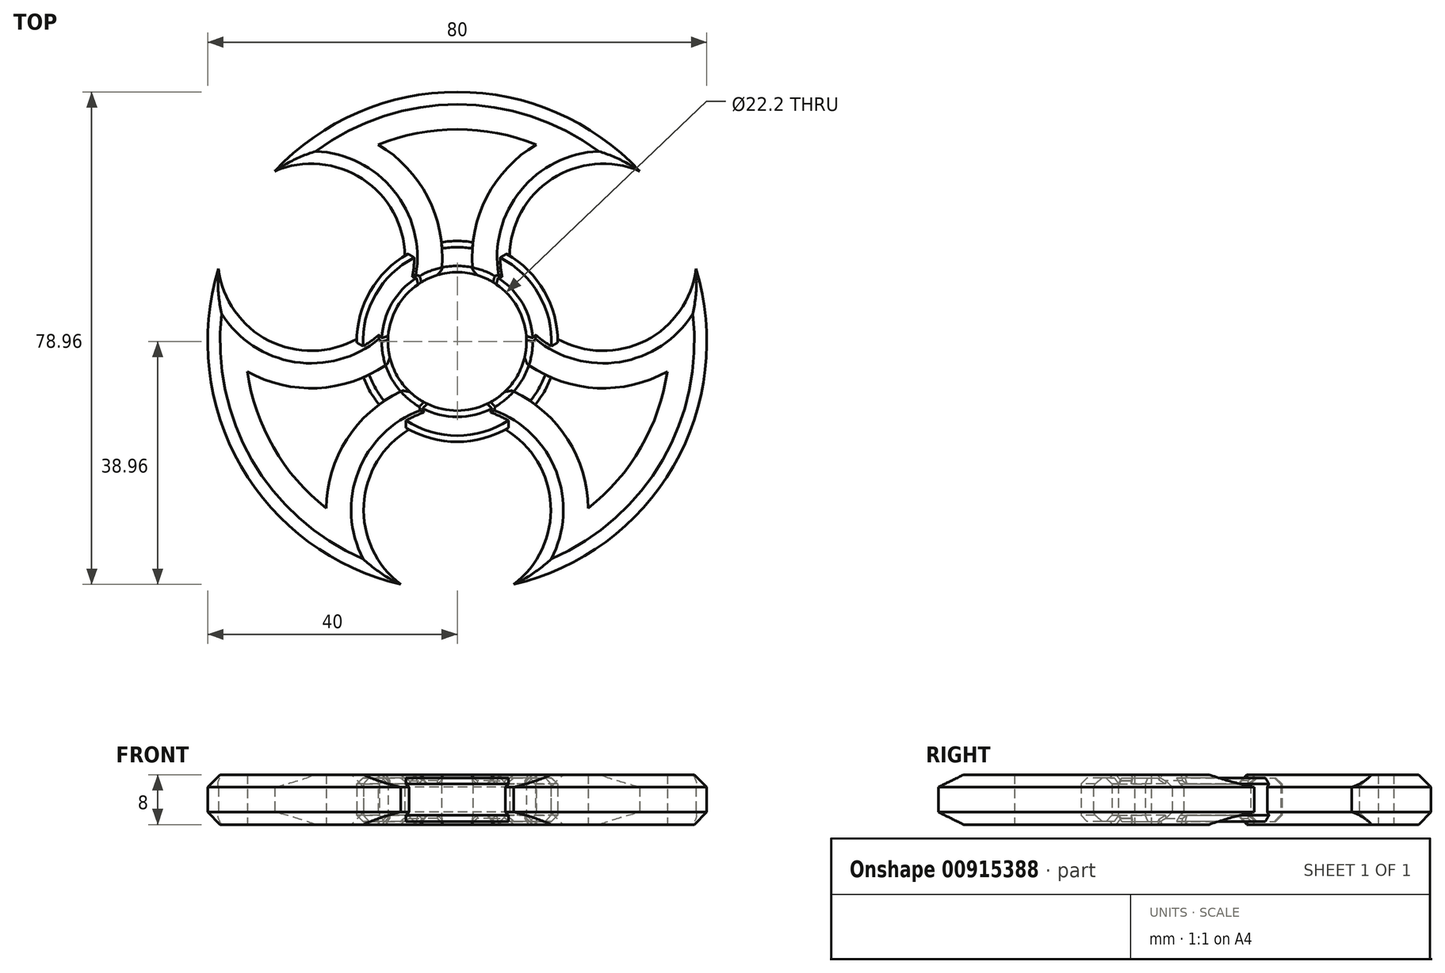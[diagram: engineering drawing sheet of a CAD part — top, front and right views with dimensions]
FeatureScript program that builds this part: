
annotation { "Feature Type Name" : "Feature", "Feature Type Description" : "" }
export const myFeature = defineFeature(function(context is Context, id is Id, definition is map)
    precondition{}
    {
        {
            var Q0;
            Q0=qCreatedBy(makeId("Top.planeOp"),FACE);
            var sketch = newSketch(context, id + "F0", { "sketchPlane" : qUnion([Q0])});
            skArc(sketch, "E0", {"start": v(29.22, 27.32) * mm, "mid": v(0, 40) * mm, "end": v(-29.22, 27.32) * mm});
            skArc(sketch, "E1", {"start": v(9.05, -38.96) * mm, "mid": v(0, -12) * mm, "end": v(-9.05, -38.96) * mm});
            skArc(sketch, "E2.1.0", {"start": v(29.22, 27.32) * mm, "mid": v(10.4, 6) * mm, "end": v(38.27, 11.64) * mm});
            skArc(sketch, "E2.2.0", {"start": v(-38.27, 11.64) * mm, "mid": v(-10.4, 6) * mm, "end": v(-29.22, 27.32) * mm});
            skArc(sketch, "E3.trimOffspring", {"start": v(9.05, -38.96) * mm, "mid": v(34.64, -20) * mm, "end": v(38.27, 11.64) * mm});
            skArc(sketch, "E4.trimOffspring", {"start": v(-38.27, 11.64) * mm, "mid": v(-34.64, -20) * mm, "end": v(-9.05, -38.96) * mm});
            skArc(sketch, "E5.0", {"start": v(21, -26.74) * mm, "mid": v(29.44, -17) * mm, "end": v(33.66, -4.81) * mm});
            skArc(sketch, "E5.1", {"start": v(-33.66, -4.81) * mm, "mid": v(-29.44, -17) * mm, "end": v(-21, -26.74) * mm});
            skArc(sketch, "E5.2", {"start": v(-33.66, -4.81) * mm, "mid": v(-5.2, 3) * mm, "end": v(-12.66, 31.56) * mm});
            skArc(sketch, "E5.3", {"start": v(21, -26.74) * mm, "mid": v(0, -6) * mm, "end": v(-21, -26.74) * mm});
            skArc(sketch, "E5.4", {"start": v(12.66, 31.56) * mm, "mid": v(0, 34) * mm, "end": v(-12.66, 31.56) * mm});
            skArc(sketch, "E5.5", {"start": v(12.66, 31.56) * mm, "mid": v(5.2, 3) * mm, "end": v(33.66, -4.81) * mm});
            skSolve(sketch);
        }
        {
            var Q0;
            Q0=makeQuery(id+"F0.imprint","IMPRINT",FACE,{"disambiguationData":[TD([[makeQuery(id+"F0.imprint","IMPRINT",EDGE,{"derivedFrom":sQuery(id+"F0.wireOp",EDGE,"E0")}),1.0]])]});
            extrude(context, id + "F1", {"entities" : qUnion([Q0]), "endBound" : BoundingType.SYMMETRIC, "depth" : 8 * mm, "offsetDistance" : 25 * mm});
        }
        {
            var Q0;
            Q0=qCreatedBy(makeId("Top.planeOp"),FACE);
            var sketch = newSketch(context, id + "F2", { "sketchPlane" : qUnion([Q0])});
            skCircle(sketch, "E6", {"center": v(0, 0) * mm, "radius": 11.1 * mm});
            skCircle(sketch, "E7", {"center": v(0, 0) * mm, "radius": 16.1 * mm});
            skSolve(sketch);
        }
        {
            var Q0;
            Q0=makeQuery(id+"F2.imprint","IMPRINT",FACE,{"disambiguationData":[TD([[makeQuery(id+"F2.imprint","IMPRINT",EDGE,{"derivedFrom":sQuery(id+"F2.wireOp",EDGE,"E6")}),-1.0]])]});
            extrude(context, id + "F3", {"entities" : qUnion([Q0]), "operationType" : NewBodyOperationType.ADD, "endBound" : BoundingType.SYMMETRIC, "depth" : 7 * mm, "offsetDistance" : 25 * mm});
        }
        {
            var Q0;
            Q0=qCreatedBy(makeId("Top.planeOp"),FACE);
            var sketch = newSketch(context, id + "F4", { "sketchPlane" : qUnion([Q0])});
            skCircle(sketch, "E8", {"center": v(0, 0) * mm, "radius": 11.1 * mm});
            skSolve(sketch);
        }
        {
            var Q0;
            Q0 = qSketchRegion(id + "F4", true);
            extrude(context, id + "F5", {"entities" : qUnion([Q0]), "operationType" : NewBodyOperationType.REMOVE, "endBound" : BoundingType.SYMMETRIC, "depth" : 10 * mm, "offsetDistance" : 25 * mm});
        }
        {
            var Q0;
            Q0=makeQuery(id+"F1.opExtrude","CAP_EDGE",EDGE,{"disambiguationData":[OSD([sQuery(id+"F0.wireOp",EDGE,"E3.trimOffspring")])],"isStart":false});
            var Q1;
            Q1=makeQuery(id+"F1.opExtrude","CAP_EDGE",EDGE,{"disambiguationData":[OSD([sQuery(id+"F0.wireOp",EDGE,"E4.trimOffspring")])],"isStart":false});
            var Q2;
            Q2=makeQuery(id+"F1.opExtrude","CAP_EDGE",EDGE,{"disambiguationData":[OSD([sQuery(id+"F0.wireOp",EDGE,"E0")])],"isStart":false});
            var Q3;
            Q3=makeQuery(id+"F1.opExtrude","CAP_EDGE",EDGE,{"disambiguationData":[OSD([sQuery(id+"F0.wireOp",EDGE,"E2.2.0")])],"isStart":false});
            var Q4;
            Q4=makeQuery(id+"F1.opExtrude","CAP_EDGE",EDGE,{"disambiguationData":[OSD([sQuery(id+"F0.wireOp",EDGE,"E2.1.0")])],"isStart":false});
            var Q5;
            Q5=makeQuery(id+"F1.opExtrude","CAP_EDGE",EDGE,{"disambiguationData":[OSD([sQuery(id+"F0.wireOp",EDGE,"E1")])],"isStart":false});
            var Q6;
            Q6=makeQuery(id+"F1.opExtrude","CAP_EDGE",EDGE,{"disambiguationData":[OSD([sQuery(id+"F0.wireOp",EDGE,"E4.trimOffspring")])],"isStart":true});
            var Q7;
            Q7=makeQuery(id+"F1.opExtrude","CAP_EDGE",EDGE,{"disambiguationData":[OSD([sQuery(id+"F0.wireOp",EDGE,"E3.trimOffspring")])],"isStart":true});
            var Q8;
            Q8=makeQuery(id+"F1.opExtrude","CAP_EDGE",EDGE,{"disambiguationData":[OSD([sQuery(id+"F0.wireOp",EDGE,"E0")])],"isStart":true});
            var Q9;
            Q9=makeQuery(id+"F1.opExtrude","CAP_EDGE",EDGE,{"disambiguationData":[OSD([sQuery(id+"F0.wireOp",EDGE,"E2.2.0")])],"isStart":true});
            var Q10;
            Q10=makeQuery(id+"F1.opExtrude","CAP_EDGE",EDGE,{"disambiguationData":[OSD([sQuery(id+"F0.wireOp",EDGE,"E1")])],"isStart":true});
            var Q11;
            Q11=makeQuery(id+"F1.opExtrude","CAP_EDGE",EDGE,{"disambiguationData":[OSD([sQuery(id+"F0.wireOp",EDGE,"E2.1.0")])],"isStart":true});
            chamfer(context, id + "F6", {"entities" : qUnion([Q0, Q1, Q2, Q3, Q4, Q5, Q6, Q7, Q8, Q9, Q10, Q11]), "width" : 2 * mm, "tangentPropagation" : true});
        }
        {
            var Q0;
            {var subQ0=makeQuery(id+"F1.opExtrude","SWEPT_FACE",FACE,{"disambiguationData":[OSD([sQuery(id+"F0.wireOp",EDGE,"E5.3")])]});var subQ1=sQuery(id+"F2.wireOp",EDGE,"E7");var subQ2=sQuery(id+"F2.wireOp",EDGE,"E6");var subQ3=makeQuery(id+"F3.opExtrude","CAP_FACE",FACE,{"disambiguationData":[OSD([subQ2,subQ1])],"isStart":false});var subQ4=makeQuery(id+"F1.opExtrude","SWEPT_FACE",FACE,{"disambiguationData":[OSD([sQuery(id+"F0.wireOp",EDGE,"E5.5")])]});var subQ5=makeQuery(id+"F3.opExtrude","CAP_FACE",FACE,{"disambiguationData":[OSD([subQ2,subQ1])],"isStart":true});var subQ6=makeQuery(id+"F3.opExtrude","SWEPT_FACE",FACE,{"disambiguationData":[OSD([subQ2])]});var subQ7=makeQuery(id+"F1.opExtrude","SWEPT_FACE",FACE,{"disambiguationData":[OSD([sQuery(id+"F0.wireOp",EDGE,"E5.2")])]});Q0=makeQuery(id+"F5.boolean.opBoolean","MERGE",FACE,{"derivedFrom":[makeQuery(id+"F3.boolean.opBoolean","SPLIT",FACE,{"disambiguationData":[TD([subQ7,subQ0,subQ5,subQ3])],"derivedFrom":subQ6}),makeQuery(id+"F3.boolean.opBoolean","SPLIT",FACE,{"disambiguationData":[TD([subQ7,subQ4,subQ5,subQ3])],"derivedFrom":subQ6}),makeQuery(id+"F3.boolean.opBoolean","SPLIT",FACE,{"disambiguationData":[TD([subQ0,subQ4,subQ5,subQ3])],"derivedFrom":subQ6})],"fromTools":[makeQuery(id+"F5.opExtrude","SWEPT_FACE",FACE,{"disambiguationData":[OSD([sQuery(id+"F4.wireOp",EDGE,"E8")])]})]});}
            chamfer(context, id + "F7", {"entities" : qUnion([Q0]), "width" : 1 * mm, "tangentPropagation" : true});
        }
        {
            var Q0;
            {var subQ0=sQuery(id+"F2.wireOp",EDGE,"E7");Q0=makeQuery(id+"F3.boolean.opBoolean","SPLIT",EDGE,{"disambiguationData":[TD([makeQuery(id+"F1.opExtrude","SWEPT_FACE",FACE,{"disambiguationData":[OSD([sQuery(id+"F0.wireOp",EDGE,"E1")])]}),makeQuery(id+"F3.opExtrude","CAP_FACE",FACE,{"disambiguationData":[OSD([sQuery(id+"F2.wireOp",EDGE,"E6"),subQ0])],"isStart":true}),makeQuery(id+"F3.opExtrude","SWEPT_FACE",FACE,{"disambiguationData":[OSD([subQ0])]})])],"derivedFrom":makeQuery(id+"F3.opExtrude","CAP_EDGE",EDGE,{"disambiguationData":[OSD([subQ0])],"isStart":true})});}
            var Q1;
            {var subQ0=sQuery(id+"F2.wireOp",EDGE,"E7");Q1=makeQuery(id+"F3.boolean.opBoolean","SPLIT",EDGE,{"disambiguationData":[TD([makeQuery(id+"F1.opExtrude","SWEPT_FACE",FACE,{"disambiguationData":[OSD([sQuery(id+"F0.wireOp",EDGE,"E2.1.0")])]}),makeQuery(id+"F3.opExtrude","CAP_FACE",FACE,{"disambiguationData":[OSD([sQuery(id+"F2.wireOp",EDGE,"E6"),subQ0])],"isStart":true}),makeQuery(id+"F3.opExtrude","SWEPT_FACE",FACE,{"disambiguationData":[OSD([subQ0])]})])],"derivedFrom":makeQuery(id+"F3.opExtrude","CAP_EDGE",EDGE,{"disambiguationData":[OSD([subQ0])],"isStart":true})});}
            var Q2;
            {var subQ0=sQuery(id+"F2.wireOp",EDGE,"E7");Q2=makeQuery(id+"F3.boolean.opBoolean","SPLIT",EDGE,{"disambiguationData":[TD([makeQuery(id+"F1.opExtrude","SWEPT_FACE",FACE,{"disambiguationData":[OSD([sQuery(id+"F0.wireOp",EDGE,"E2.2.0")])]}),makeQuery(id+"F3.opExtrude","CAP_FACE",FACE,{"disambiguationData":[OSD([sQuery(id+"F2.wireOp",EDGE,"E6"),subQ0])],"isStart":true}),makeQuery(id+"F3.opExtrude","SWEPT_FACE",FACE,{"disambiguationData":[OSD([subQ0])]})])],"derivedFrom":makeQuery(id+"F3.opExtrude","CAP_EDGE",EDGE,{"disambiguationData":[OSD([subQ0])],"isStart":true})});}
            var Q3;
            {var subQ0=sQuery(id+"F2.wireOp",EDGE,"E7");Q3=makeQuery(id+"F3.boolean.opBoolean","SPLIT",EDGE,{"disambiguationData":[TD([makeQuery(id+"F1.opExtrude","SWEPT_FACE",FACE,{"disambiguationData":[OSD([sQuery(id+"F0.wireOp",EDGE,"E5.2")])]}),makeQuery(id+"F1.opExtrude","SWEPT_FACE",FACE,{"disambiguationData":[OSD([sQuery(id+"F0.wireOp",EDGE,"E5.5")])]}),makeQuery(id+"F3.opExtrude","CAP_FACE",FACE,{"disambiguationData":[OSD([sQuery(id+"F2.wireOp",EDGE,"E6"),subQ0])],"isStart":true}),makeQuery(id+"F3.opExtrude","SWEPT_FACE",FACE,{"disambiguationData":[OSD([subQ0])]})])],"derivedFrom":makeQuery(id+"F3.opExtrude","CAP_EDGE",EDGE,{"disambiguationData":[OSD([subQ0])],"isStart":true})});}
            var Q4;
            {var subQ0=sQuery(id+"F2.wireOp",EDGE,"E7");Q4=makeQuery(id+"F3.boolean.opBoolean","SPLIT",EDGE,{"disambiguationData":[TD([makeQuery(id+"F1.opExtrude","SWEPT_FACE",FACE,{"disambiguationData":[OSD([sQuery(id+"F0.wireOp",EDGE,"E5.3")])]}),makeQuery(id+"F1.opExtrude","SWEPT_FACE",FACE,{"disambiguationData":[OSD([sQuery(id+"F0.wireOp",EDGE,"E5.5")])]}),makeQuery(id+"F3.opExtrude","CAP_FACE",FACE,{"disambiguationData":[OSD([sQuery(id+"F2.wireOp",EDGE,"E6"),subQ0])],"isStart":true}),makeQuery(id+"F3.opExtrude","SWEPT_FACE",FACE,{"disambiguationData":[OSD([subQ0])]})])],"derivedFrom":makeQuery(id+"F3.opExtrude","CAP_EDGE",EDGE,{"disambiguationData":[OSD([subQ0])],"isStart":true})});}
            var Q5;
            {var subQ0=sQuery(id+"F2.wireOp",EDGE,"E7");Q5=makeQuery(id+"F3.boolean.opBoolean","SPLIT",EDGE,{"disambiguationData":[TD([makeQuery(id+"F1.opExtrude","SWEPT_FACE",FACE,{"disambiguationData":[OSD([sQuery(id+"F0.wireOp",EDGE,"E5.2")])]}),makeQuery(id+"F1.opExtrude","SWEPT_FACE",FACE,{"disambiguationData":[OSD([sQuery(id+"F0.wireOp",EDGE,"E5.3")])]}),makeQuery(id+"F3.opExtrude","CAP_FACE",FACE,{"disambiguationData":[OSD([sQuery(id+"F2.wireOp",EDGE,"E6"),subQ0])],"isStart":true}),makeQuery(id+"F3.opExtrude","SWEPT_FACE",FACE,{"disambiguationData":[OSD([subQ0])]})])],"derivedFrom":makeQuery(id+"F3.opExtrude","CAP_EDGE",EDGE,{"disambiguationData":[OSD([subQ0])],"isStart":true})});}
            var Q6;
            {var subQ0=sQuery(id+"F2.wireOp",EDGE,"E7");Q6=makeQuery(id+"F3.boolean.opBoolean","SPLIT",EDGE,{"disambiguationData":[TD([makeQuery(id+"F1.opExtrude","SWEPT_FACE",FACE,{"disambiguationData":[OSD([sQuery(id+"F0.wireOp",EDGE,"E2.2.0")])]}),makeQuery(id+"F3.opExtrude","CAP_FACE",FACE,{"disambiguationData":[OSD([sQuery(id+"F2.wireOp",EDGE,"E6"),subQ0])],"isStart":false}),makeQuery(id+"F3.opExtrude","SWEPT_FACE",FACE,{"disambiguationData":[OSD([subQ0])]})])],"derivedFrom":makeQuery(id+"F3.opExtrude","CAP_EDGE",EDGE,{"disambiguationData":[OSD([subQ0])],"isStart":false})});}
            var Q7;
            {var subQ0=sQuery(id+"F2.wireOp",EDGE,"E7");Q7=makeQuery(id+"F3.boolean.opBoolean","SPLIT",EDGE,{"disambiguationData":[TD([makeQuery(id+"F1.opExtrude","SWEPT_FACE",FACE,{"disambiguationData":[OSD([sQuery(id+"F0.wireOp",EDGE,"E2.1.0")])]}),makeQuery(id+"F3.opExtrude","CAP_FACE",FACE,{"disambiguationData":[OSD([sQuery(id+"F2.wireOp",EDGE,"E6"),subQ0])],"isStart":false}),makeQuery(id+"F3.opExtrude","SWEPT_FACE",FACE,{"disambiguationData":[OSD([subQ0])]})])],"derivedFrom":makeQuery(id+"F3.opExtrude","CAP_EDGE",EDGE,{"disambiguationData":[OSD([subQ0])],"isStart":false})});}
            var Q8;
            {var subQ0=sQuery(id+"F2.wireOp",EDGE,"E7");Q8=makeQuery(id+"F3.boolean.opBoolean","SPLIT",EDGE,{"disambiguationData":[TD([makeQuery(id+"F1.opExtrude","SWEPT_FACE",FACE,{"disambiguationData":[OSD([sQuery(id+"F0.wireOp",EDGE,"E1")])]}),makeQuery(id+"F3.opExtrude","CAP_FACE",FACE,{"disambiguationData":[OSD([sQuery(id+"F2.wireOp",EDGE,"E6"),subQ0])],"isStart":false}),makeQuery(id+"F3.opExtrude","SWEPT_FACE",FACE,{"disambiguationData":[OSD([subQ0])]})])],"derivedFrom":makeQuery(id+"F3.opExtrude","CAP_EDGE",EDGE,{"disambiguationData":[OSD([subQ0])],"isStart":false})});}
            var Q9;
            {var subQ0=sQuery(id+"F2.wireOp",EDGE,"E7");Q9=makeQuery(id+"F3.boolean.opBoolean","SPLIT",EDGE,{"disambiguationData":[TD([makeQuery(id+"F1.opExtrude","SWEPT_FACE",FACE,{"disambiguationData":[OSD([sQuery(id+"F0.wireOp",EDGE,"E5.3")])]}),makeQuery(id+"F1.opExtrude","SWEPT_FACE",FACE,{"disambiguationData":[OSD([sQuery(id+"F0.wireOp",EDGE,"E5.5")])]}),makeQuery(id+"F3.opExtrude","CAP_FACE",FACE,{"disambiguationData":[OSD([sQuery(id+"F2.wireOp",EDGE,"E6"),subQ0])],"isStart":false}),makeQuery(id+"F3.opExtrude","SWEPT_FACE",FACE,{"disambiguationData":[OSD([subQ0])]})])],"derivedFrom":makeQuery(id+"F3.opExtrude","CAP_EDGE",EDGE,{"disambiguationData":[OSD([subQ0])],"isStart":false})});}
            var Q10;
            {var subQ0=sQuery(id+"F2.wireOp",EDGE,"E7");Q10=makeQuery(id+"F3.boolean.opBoolean","SPLIT",EDGE,{"disambiguationData":[TD([makeQuery(id+"F1.opExtrude","SWEPT_FACE",FACE,{"disambiguationData":[OSD([sQuery(id+"F0.wireOp",EDGE,"E5.2")])]}),makeQuery(id+"F1.opExtrude","SWEPT_FACE",FACE,{"disambiguationData":[OSD([sQuery(id+"F0.wireOp",EDGE,"E5.3")])]}),makeQuery(id+"F3.opExtrude","CAP_FACE",FACE,{"disambiguationData":[OSD([sQuery(id+"F2.wireOp",EDGE,"E6"),subQ0])],"isStart":false}),makeQuery(id+"F3.opExtrude","SWEPT_FACE",FACE,{"disambiguationData":[OSD([subQ0])]})])],"derivedFrom":makeQuery(id+"F3.opExtrude","CAP_EDGE",EDGE,{"disambiguationData":[OSD([subQ0])],"isStart":false})});}
            var Q11;
            {var subQ0=sQuery(id+"F2.wireOp",EDGE,"E7");Q11=makeQuery(id+"F3.boolean.opBoolean","SPLIT",EDGE,{"disambiguationData":[TD([makeQuery(id+"F1.opExtrude","SWEPT_FACE",FACE,{"disambiguationData":[OSD([sQuery(id+"F0.wireOp",EDGE,"E5.2")])]}),makeQuery(id+"F1.opExtrude","SWEPT_FACE",FACE,{"disambiguationData":[OSD([sQuery(id+"F0.wireOp",EDGE,"E5.5")])]}),makeQuery(id+"F3.opExtrude","CAP_FACE",FACE,{"disambiguationData":[OSD([sQuery(id+"F2.wireOp",EDGE,"E6"),subQ0])],"isStart":false}),makeQuery(id+"F3.opExtrude","SWEPT_FACE",FACE,{"disambiguationData":[OSD([subQ0])]})])],"derivedFrom":makeQuery(id+"F3.opExtrude","CAP_EDGE",EDGE,{"disambiguationData":[OSD([subQ0])],"isStart":false})});}
            chamfer(context, id + "F8", {"entities" : qUnion([Q0, Q1, Q2, Q3, Q4, Q5, Q6, Q7, Q8, Q9, Q10, Q11]), "width" : 1 * mm, "tangentPropagation" : true});
        }
    });
